# Revit family: TataSteel_Lintels_MBA
name_source: partatom
category: Generic Models
revit_build: Autodesk Revit 2015 (Build: 20140606_1530(x64)
units: mm (PartAtom-declared; Revit-internal decimal feet)

## types (1)
- TataSteel_Lintels_MBA
    AllowableLoadLimiting = 3 mm  [stored 0.00984252 ft]
    AssetType = FIXED
    BIMObjectName = TataSteel_Lintel_MBA_1350
    BIMobject category = Beams & Lintels
    CharacteristicDeflectionUnderLoad = 0 mm  [stored 0 ft]
    CharacteristicResistanceToFire = 60 mm
    CharacteristicThermalConductivity = 0 mm  [stored 0 ft]
    ClearSpan = 1050 mm
    Color = Black
    Description = Meter box angle
    Edition number = 1
    EndBearing = 150 mm  [stored 0.492126 ft]
    ExpectedLife = 60 yrs
    Finish = Galv and Powder coated
    FireRating = 60
    Grade = DX51
    IFC Classification = Structural Member
    IfcExportAs = IfcBeamType
    IfcExportType = LINTEL
    Installation instructions = http://catnic.com
    InstallationDate = 1900-12-31T23:59:59
    IsExternal = Yes
    LengthIncrement = 150mm up to 3000mm. 
300mm above 3000mm
    LintelHeight = 88 mm  [stored 0.288714 ft]
    LintelLength = 1350 mm  [stored 4.42913 ft]
    LintelOuterLeaf = 88 mm  [stored 0.288714 ft]
    LintelThickness = 2 mm  [stored 0.00656168 ft]
    LintelType = METER BOX
    LipHeight = 2 mm  [stored 0.00656168 ft]
    LipLength = 17 mm  [stored 0.0557743 ft]
    LoadBearing = Yes
    LoadCategory = LIGHT DUTY
    Manufacturer = Catnic, TATA
    Manufacturer country = United Kingdom
    Manufacturer name = Tata Steel
    ManufacturerURL = www.catnic.com
    Material main = Steel
    MaxLintelLength = 1350
    MinLintelLength = 750
    Model = TataSteel_Lintel_MBA_1350
    ModelNumber = MBA
    ModelReference = Single Leaf Walls
    NBSDescription = Pre fabricated Steel Lintel
    NBSReference = F30 755
    Name = Lintel
    Nominal height = 0
    Nominal width = 0
    NominalLength = 1350 mm  [stored 4.42913 ft]
    OmniClass Code = 23-13 21 25 11
    OmniClass Description = Lintels
    Product Guid = eda4763d-b8e1-411a-8b66-9ec8dc3e0a3a
    Product SKU = catnic-mba
    Product certification = http://catnic.com
    Product family = Lintels
    Product group = Catnic
    ProductInformation = www.catnic.com
    QR code = http://bimobject.com
    Roll = 0 mm  [stored 0 ft]
    SafeWorkingLoad = 3 mm  [stored 0.00984252 ft]
    Shape = Angle
    Size = 88H x88W x1350L
    Slope = 0 mm  [stored 0 ft]
    Span = 1050 mm
    Steel = Steel
    TSE_BIMObjectName = TataSteel_Lintel_MBA_1350
    TSE_Documentation = www.catnic.com
    TSE_InstallationInstructions = www.catnic.com
    TSE_ManufacturerURL = www.catnic.com
    TSE_Model = TataSteel_Lintel_MBA_1350
    TSE_ProductCertification = www.catnic.com
    TSE_QR code = <None>
    Technical description = http://catnic.com
    ThermalTransmittance = 0 mm  [stored 0 ft]
    Type Image = <None>
    UNSPSC Code = 30101704
    URL = www.catnic.com
    Uniclass 1.4 Code = L3241
    Uniclass 1.4 Description = Lintels
    Uniclass 2015 Code = Pr_20_85_48
    Uniclass 2015 Name = Lintels
    Uniclass2015 = Pr_20_85_48_11
    WallCavity = 50 mm  [stored 0.164042 ft]
    WallInnerLeaf = 100 mm  [stored 0.328084 ft]
    WallOuterLeaf = 102 mm
    WarrantyStartDate = 1900-12-31T23:59:59
    Weight = 2 mm  [stored 0.00656168 ft]
    Weight Net (Kg) = 0
    Youtube clip = https://youtu.be
    b1 = 127 mm
    b2 = 125 mm  [stored 0.410105 ft]
    b3 = 25 mm  [stored 0.082021 ft]
    h1 = 44 mm
    r2 = 3 mm  [stored 0.00984252 ft]
    r3 = 4 mm  [stored 0.0131234 ft]

note: [stored X ft] marks values corroborated as IEEE doubles in the binary element streams (Revit-internal decimal feet)

## geometry (parser evidence)
native form markers: Sweep x3
no freeform markers — native parametric forms only
